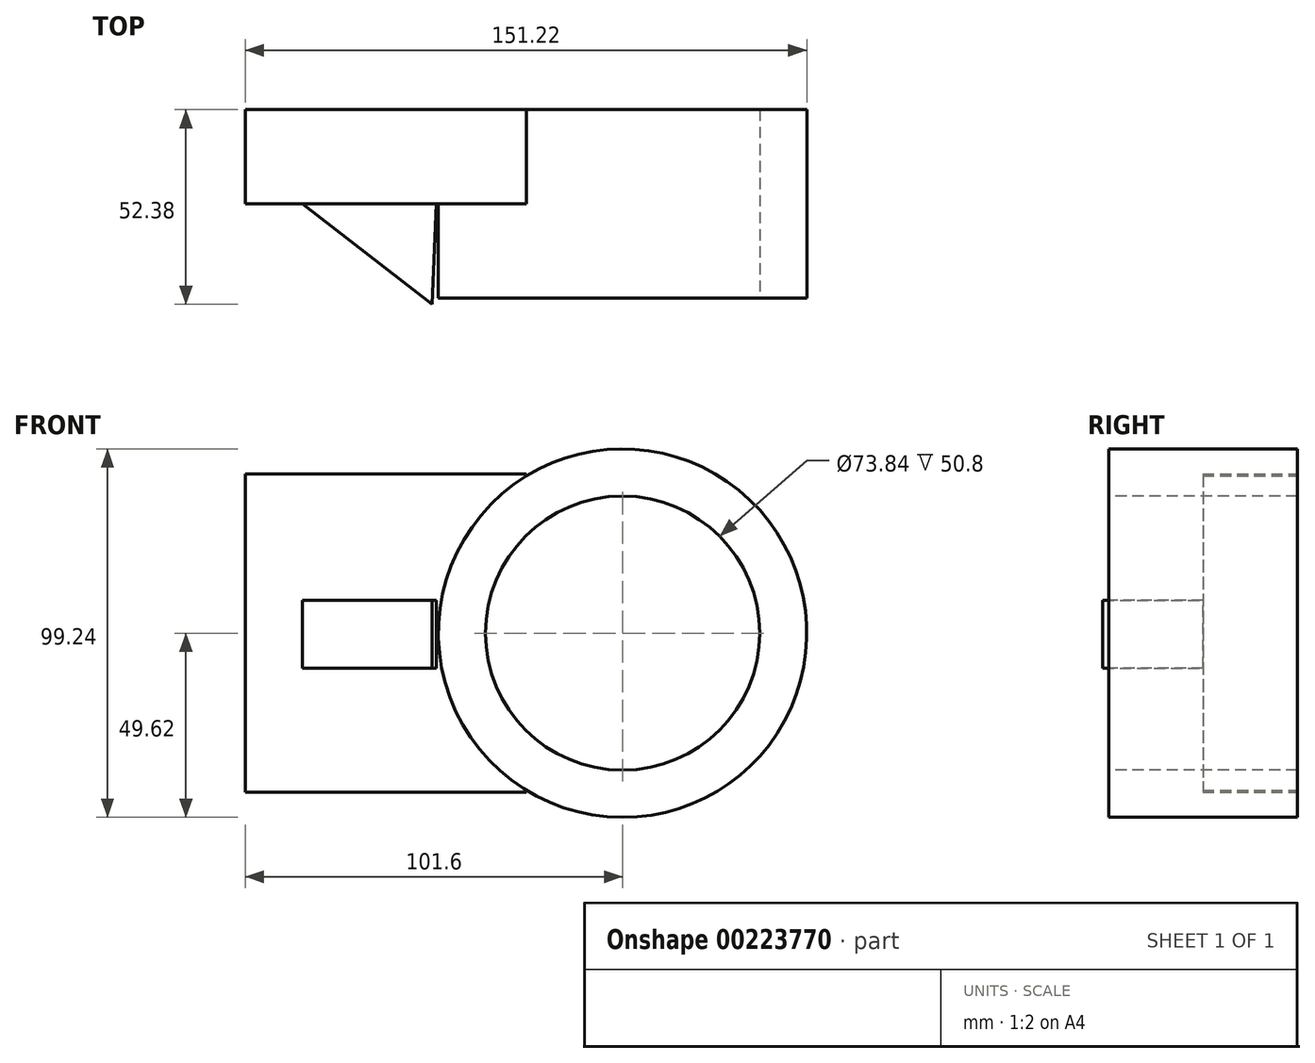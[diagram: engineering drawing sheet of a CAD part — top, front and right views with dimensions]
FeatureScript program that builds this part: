
annotation { "Feature Type Name" : "Feature", "Feature Type Description" : "" }
export const myFeature = defineFeature(function(context is Context, id is Id, definition is map)
    precondition{}
    {
        {
            var Q0;
            Q0=qCreatedBy(makeId("Front.planeOp"),FACE);
            var sketch = newSketch(context, id + "F0", { "sketchPlane" : qUnion([Q0])});
            skLineSegment(sketch, "E0.bottom", {"start": v(-76.2, 42.83) * mm, "end": v(-0.46, 42.83) * mm});
            skLineSegment(sketch, "E0.top", {"start": v(-76.2, -42.83) * mm, "end": v(-0.46, -42.83) * mm});
            skLineSegment(sketch, "E0.left", {"start": v(-76.2, 42.83) * mm, "end": v(-76.2, -42.83) * mm});
            skLineSegment(sketch, "E0.right", {"start": v(-0.46, 42.83) * mm, "end": v(-0.46, -42.83) * mm});
            skPoint(sketch, "E0.middle", {"position": v(-38.33, 0) * mm});
            skSolve(sketch);
        }
        {
            var Q0;
            Q0=qCreatedBy(makeId("Front.planeOp"),FACE);
            var sketch = newSketch(context, id + "F1", { "sketchPlane" : qUnion([Q0])});
            skCircle(sketch, "E1", {"center": v(25.4, 0) * mm, "radius": 49.62 * mm});
            skSolve(sketch);
        }
        {
            var Q0;
            Q0=makeQuery(id+"F0.imprint","IMPRINT",FACE,{"disambiguationData":[TD([[makeQuery(id+"F0.imprint","IMPRINT",EDGE,{"derivedFrom":sQuery(id+"F0.wireOp",EDGE,"E0.bottom")}),-1.0]])]});
            extrude(context, id + "F2", {"entities" : qUnion([Q0]), "depth" : 25.4 * mm});
        }
        {
            var Q0;
            Q0=makeQuery(id+"F1.imprint","IMPRINT",FACE,{"disambiguationData":[TD([[makeQuery(id+"F1.imprint","IMPRINT",EDGE,{"derivedFrom":sQuery(id+"F1.wireOp",EDGE,"E1")}),1.0]])]});
            extrude(context, id + "F3", {"entities" : qUnion([Q0]), "operationType" : NewBodyOperationType.ADD, "depth" : 50.8 * mm});
        }
        {
            var Q0;
            Q0=makeQuery(id+"F3.opExtrude","CAP_FACE",FACE,{"disambiguationData":[OSD([sQuery(id+"F1.wireOp",EDGE,"E1")])],"isStart":false});
            var sketch = newSketch(context, id + "F4", { "sketchPlane" : qUnion([Q0])});
            skCircle(sketch, "E2", {"center": v(25.4, 0) * mm, "radius": 36.92 * mm});
            skSolve(sketch);
        }
        {
            var Q0;
            Q0=makeQuery(id+"F4.imprint","IMPRINT",FACE,{"disambiguationData":[TD([[makeQuery(id+"F4.imprint","IMPRINT",EDGE,{"derivedFrom":sQuery(id+"F4.wireOp",EDGE,"E2")}),1.0]])]});
            extrude(context, id + "F5", {"entities" : qUnion([Q0]), "operationType" : NewBodyOperationType.REMOVE, "endBound" : BoundingType.THROUGH_ALL, "oppositeDirection" : true, "depth" : 25.4 * mm});
        }
        {
            var Q0;
            Q0=qCreatedBy(makeId("Top.planeOp"),FACE);
            var sketch = newSketch(context, id + "F6", { "sketchPlane" : qUnion([Q0])});
            skLineSegment(sketch, "E3", {"start": v(-25.9, -52.38) * mm, "end": v(-61.5, -24.9) * mm});
            skLineSegment(sketch, "E4", {"start": v(-61.5, -24.9) * mm, "end": v(-24.7, -24.9) * mm});
            skLineSegment(sketch, "E5", {"start": v(-24.7, -24.9) * mm, "end": v(-25.9, -52.38) * mm});
            skSolve(sketch);
        }
        {
            var Q0;
            Q0=makeQuery(id+"F6.imprint","IMPRINT",FACE,{"disambiguationData":[TD([[makeQuery(id+"F6.imprint","IMPRINT",EDGE,{"derivedFrom":sQuery(id+"F6.wireOp",EDGE,"E3")}),-1.0]])]});
            extrude(context, id + "F7", {"entities" : qUnion([Q0]), "operationType" : NewBodyOperationType.ADD, "depth" : 8.9 * mm, "hasSecondDirection" : true, "secondDirectionOppositeDirection" : true, "secondDirectionDepth" : 9.4 * mm});
        }
    });
